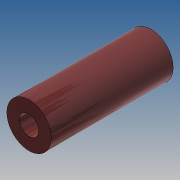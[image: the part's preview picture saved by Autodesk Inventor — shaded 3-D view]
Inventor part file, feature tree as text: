
AUTODESK INVENTOR PART (.ipt)
format: ipt  version: 2017 (Build 210142000, 142)  size: 87,040 bytes
history: native  units: mm
features: other x1, extrude x1, sketch x1
ambient origin geometry x8: Origin, YZ Plane, XZ Plane, XY Plane, X Axis, Y Axis, Z Axis, Center Point
bodies: Body1 (feature_tree)
feature tree (3):
  other  "Sólido1"
  extrude  "Extrusión1"  Depth=22.0mm
  sketch  "Boceto1"  dims[d0=3.5mm d1=8.0mm d2=22.0mm d3=0.0mm]
